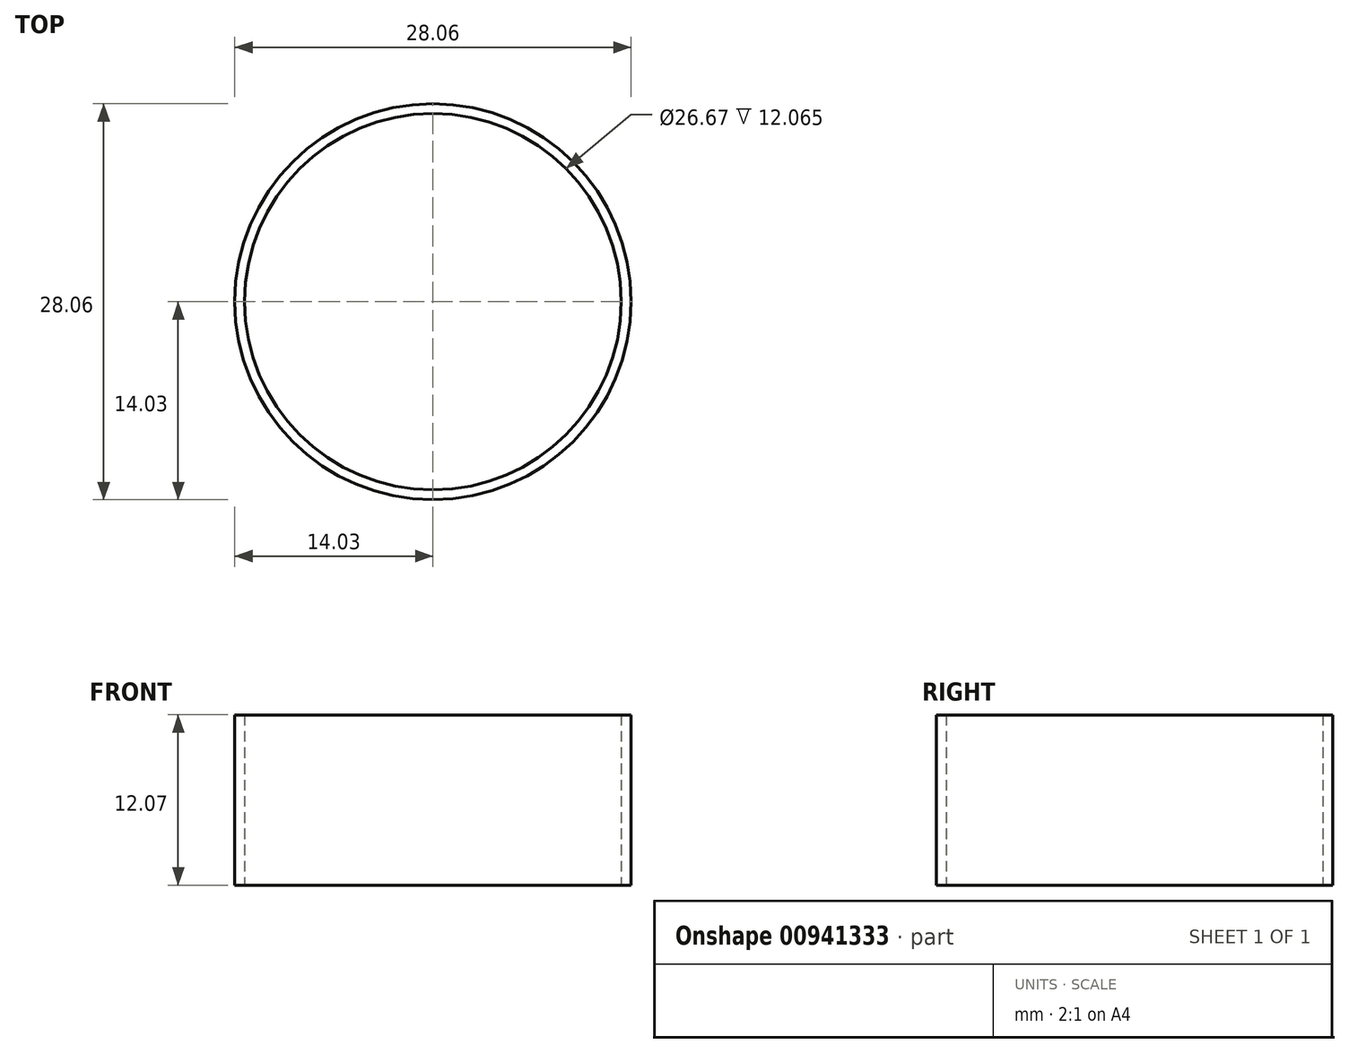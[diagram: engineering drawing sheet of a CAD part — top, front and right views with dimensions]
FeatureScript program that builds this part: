
annotation { "Feature Type Name" : "Feature", "Feature Type Description" : "" }
export const myFeature = defineFeature(function(context is Context, id is Id, definition is map)
    precondition{}
    {
        {
            var Q0;
            Q0=qCreatedBy(makeId("Top.planeOp"),FACE);
            var sketch = newSketch(context, id + "F0", { "sketchPlane" : qUnion([Q0])});
            skCircle(sketch, "E0", {"center": v(0, 0) * mm, "radius": 14.03 * mm});
            skCircle(sketch, "E1", {"center": v(0, 0) * mm, "radius": 13.34 * mm});
            skSolve(sketch);
        }
        {
            var Q0;
            Q0=makeQuery(id+"F0.imprint","IMPRINT",FACE,{"disambiguationData":[TD([[makeQuery(id+"F0.imprint","IMPRINT",EDGE,{"derivedFrom":sQuery(id+"F0.wireOp",EDGE,"E0")}),1.0]])]});
            extrude(context, id + "F1", {"entities" : qUnion([Q0]), "depth" : 12.06 * mm, "offsetDistance" : 25.4 * mm});
        }
    });
